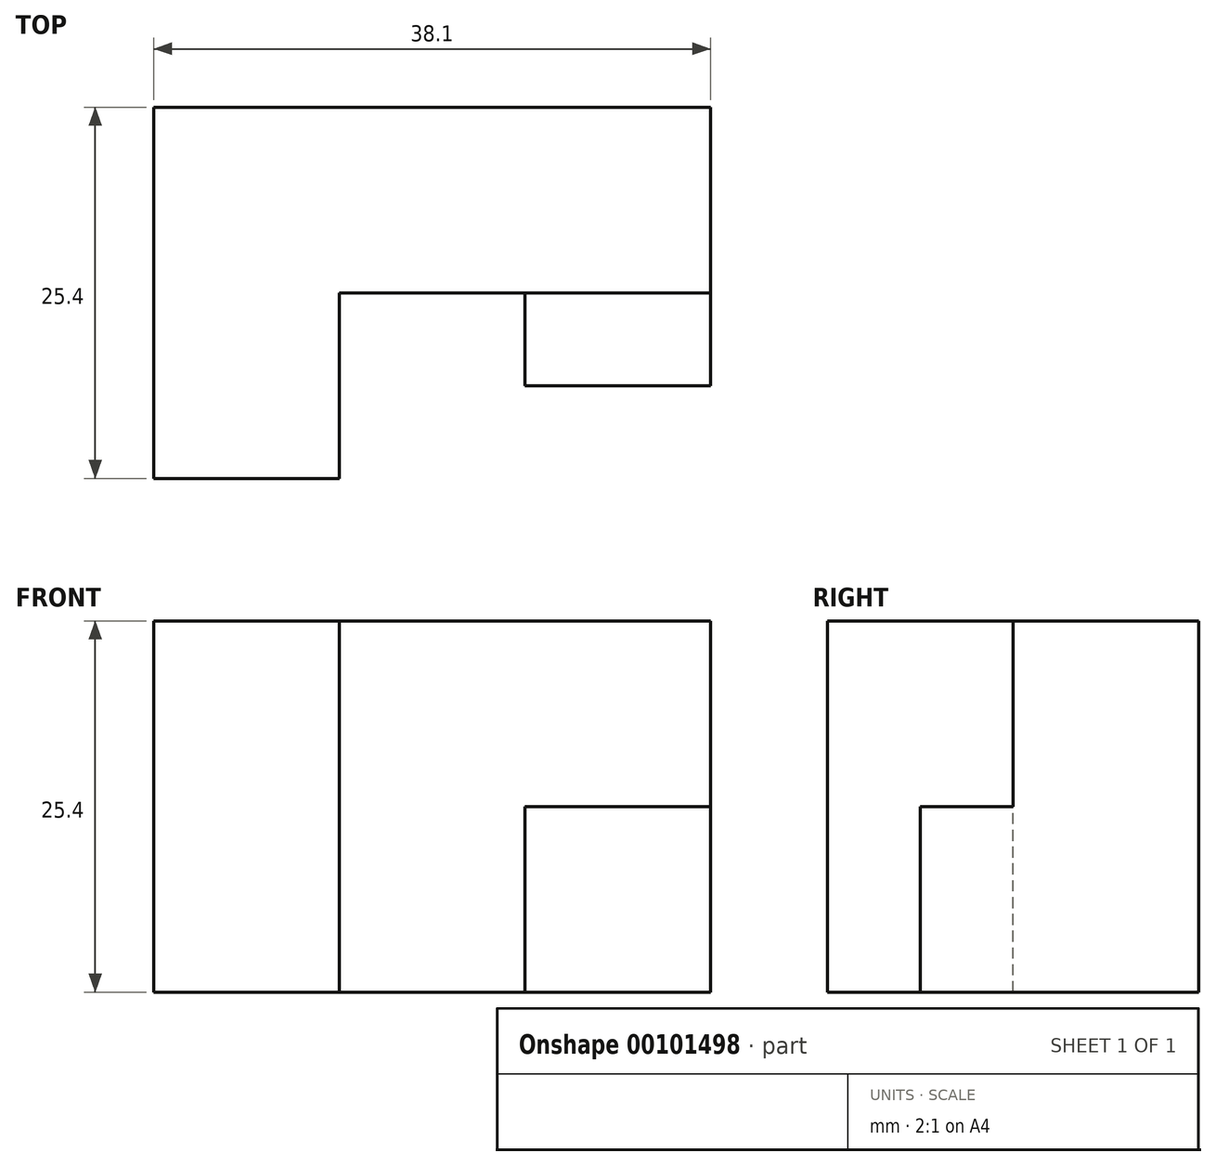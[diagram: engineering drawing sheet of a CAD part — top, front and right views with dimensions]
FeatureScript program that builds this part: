
annotation { "Feature Type Name" : "Feature", "Feature Type Description" : "" }
export const myFeature = defineFeature(function(context is Context, id is Id, definition is map)
    precondition{}
    {
        {
            var Q0;
            Q0=qCreatedBy(makeId("Top.planeOp"),FACE);
            var sketch = newSketch(context, id + "F0", { "sketchPlane" : qUnion([Q0])});
            skLineSegment(sketch, "E0", {"start": v(0, 0) * mm, "end": v(0, 25.4) * mm});
            skLineSegment(sketch, "E1", {"start": v(0, 25.4) * mm, "end": v(38.1, 25.4) * mm});
            skLineSegment(sketch, "E2", {"start": v(38.1, 25.4) * mm, "end": v(38.1, 12.7) * mm});
            skLineSegment(sketch, "E3", {"start": v(38.1, 12.7) * mm, "end": v(12.7, 12.7) * mm});
            skLineSegment(sketch, "E4", {"start": v(12.7, 12.7) * mm, "end": v(12.7, 0) * mm});
            skLineSegment(sketch, "E5", {"start": v(12.7, 0) * mm, "end": v(0, 0) * mm});
            skSolve(sketch);
        }
        {
            var Q0;
            Q0=makeQuery(id+"F0.imprint","IMPRINT",FACE,{"disambiguationData":[TD([[makeQuery(id+"F0.imprint","IMPRINT",EDGE,{"derivedFrom":sQuery(id+"F0.wireOp",EDGE,"E0")}),-1.0]])]});
            extrude(context, id + "F1", {"entities" : qUnion([Q0]), "depth" : 25.4 * mm});
        }
        {
            var Q0;
            Q0=makeQuery(id+"F1.opExtrude","SWEPT_FACE",FACE,{"disambiguationData":[OSD([sQuery(id+"F0.wireOp",EDGE,"E3")])]});
            var sketch = newSketch(context, id + "F2", { "sketchPlane" : qUnion([Q0])});
            skLineSegment(sketch, "E6", {"start": v(25.4, 0) * mm, "end": v(25.4, 12.7) * mm});
            skPoint(sketch, "E6.endSnap0", {"position": v(38.1, 12.7) * mm});
            skLineSegment(sketch, "E7", {"start": v(25.4, 12.7) * mm, "end": v(38.1, 12.7) * mm});
            skSolve(sketch);
        }
        {
            var Q0;
            {var subQ0=sQuery(id+"F2.wireOp",EDGE,"E6");Q0=makeQuery(id+"F2.imprint","IMPRINT",FACE,{"disambiguationData":[TD([[makeQuery(id+"F2.imprint","IMPRINT",EDGE,{"derivedFrom":subQ0}),-1.0]])]});}
            extrude(context, id + "F3", {"entities" : qUnion([Q0]), "operationType" : NewBodyOperationType.ADD, "depth" : 6.35 * mm});
        }
    });
